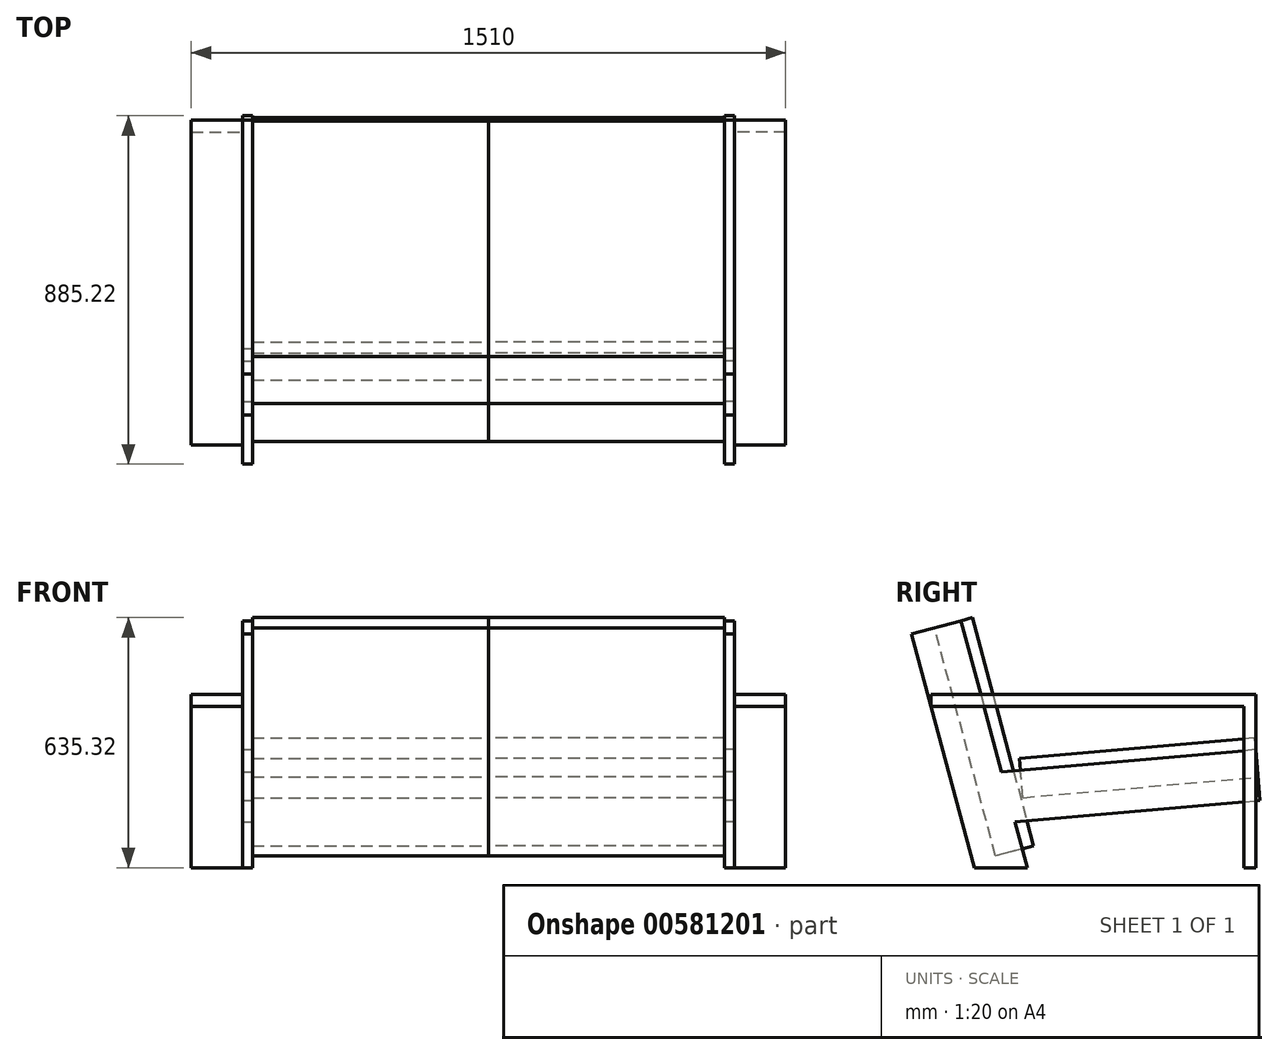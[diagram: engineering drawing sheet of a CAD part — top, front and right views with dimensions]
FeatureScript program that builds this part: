
annotation { "Feature Type Name" : "Feature", "Feature Type Description" : "" }
export const myFeature = defineFeature(function(context is Context, id is Id, definition is map)
    precondition{}
    {
        {
            var Q0;
            Q0=qCreatedBy(makeId("Right.planeOp"),FACE);
            var sketch = newSketch(context, id + "F0", { "sketchPlane" : qUnion([Q0])});
            skLineSegment(sketch, "E0", {"start": v(0, 0) * mm, "end": v(597.72, 52.3) * mm});
            skLineSegment(sketch, "E1", {"start": v(597.72, 52.3) * mm, "end": v(589, 151.91) * mm});
            skLineSegment(sketch, "E2", {"start": v(589, 151.91) * mm, "end": v(-8.72, 99.62) * mm});
            skLineSegment(sketch, "E3", {"start": v(0, 0) * mm, "end": v(-8.72, 99.62) * mm});
            skPoint(sketch, "E4.orphan", {"position": v(0, 100.38) * mm});
            skLineSegment(sketch, "E5", {"start": v(0, 0) * mm, "end": v(456.46, 0) * mm, "construction": true});
            skLineSegment(sketch, "E6", {"start": v(-127.72, 457.35) * mm, "end": v(27.57, -122.2) * mm});
            skLineSegment(sketch, "E7", {"start": v(27.57, -122.2) * mm, "end": v(-69.02, -148.09) * mm});
            skLineSegment(sketch, "E8", {"start": v(-69.02, -148.09) * mm, "end": v(-224.32, 431.47) * mm});
            skLineSegment(sketch, "E9", {"start": v(-127.72, 457.35) * mm, "end": v(-224.32, 431.47) * mm});
            skSolve(sketch);
        }
        {
            var Q0;
            Q0 = qSketchRegion(id + "F0", true);
            extrude(context, id + "F1", {"entities" : qUnion([Q0]), "depth" : 600 * mm, "offsetDistance" : 25 * mm});
        }
        {
            var Q0;
            Q0=makeQuery(id+"F1.opExtrude","CAP_FACE",FACE,{"disambiguationData":[OSD([sQuery(id+"F0.wireOp",EDGE,"E0"),sQuery(id+"F0.wireOp",EDGE,"E1"),sQuery(id+"F0.wireOp",EDGE,"E2"),sQuery(id+"F0.wireOp",EDGE,"E3")])],"isStart":true});
            var sketch = newSketch(context, id + "F2", { "sketchPlane" : qUnion([Q0])});
            skLineSegment(sketch, "E10.0.0", {"start": v(0, 0) * mm, "end": v(8.72, 99.62) * mm});
            skLineSegment(sketch, "E10.0.1", {"start": v(8.72, 99.62) * mm, "end": v(-589, 151.91) * mm});
            skLineSegment(sketch, "E10.0.2", {"start": v(-589, 151.91) * mm, "end": v(-597.72, 52.3) * mm});
            skLineSegment(sketch, "E10.0.3", {"start": v(-597.72, 52.3) * mm, "end": v(0, 0) * mm});
            skLineSegment(sketch, "E11.0.0", {"start": v(127.72, 457.35) * mm, "end": v(-27.57, -122.2) * mm});
            skLineSegment(sketch, "E11.0.1", {"start": v(-27.57, -122.2) * mm, "end": v(69.02, -148.09) * mm});
            skLineSegment(sketch, "E11.0.2", {"start": v(69.02, -148.09) * mm, "end": v(224.32, 431.47) * mm});
            skLineSegment(sketch, "E11.0.3", {"start": v(224.32, 431.47) * mm, "end": v(127.72, 457.35) * mm});
            skSolve(sketch);
        }
        {
            var Q0;
            Q0 = qSketchRegion(id + "F2", true);
            extrude(context, id + "F3", {"entities" : qUnion([Q0]), "depth" : 600 * mm, "offsetDistance" : 25 * mm});
        }
        {
            var Q0;
            Q0=makeQuery(id+"F1.opExtrude","CAP_FACE",FACE,{"disambiguationData":[OSD([sQuery(id+"F0.wireOp",EDGE,"E0"),sQuery(id+"F0.wireOp",EDGE,"E1"),sQuery(id+"F0.wireOp",EDGE,"E2"),sQuery(id+"F0.wireOp",EDGE,"E3")])],"isStart":false});
            var sketch = newSketch(context, id + "F4", { "sketchPlane" : qUnion([Q0])});
            skLineSegment(sketch, "E12", {"start": v(-156.7, 449.59) * mm, "end": v(-282.27, 415.94) * mm});
            skLineSegment(sketch, "E13", {"start": v(-156.7, 449.59) * mm, "end": v(11.45, -177.97) * mm});
            skLineSegment(sketch, "E14", {"start": v(-282.27, 415.94) * mm, "end": v(-123.13, -177.97) * mm});
            skLineSegment(sketch, "E15", {"start": v(-123.13, -177.97) * mm, "end": v(11.45, -177.97) * mm});
            skLineSegment(sketch, "E16", {"start": v(-19.64, -61.95) * mm, "end": v(602.95, -7.48) * mm});
            skLineSegment(sketch, "E17", {"start": v(602.95, -7.48) * mm, "end": v(591.62, 122.03) * mm});
            skLineSegment(sketch, "E18", {"start": v(591.62, 122.03) * mm, "end": v(-53.8, 65.56) * mm});
            skSolve(sketch);
        }
        {
            var Q0;
            Q0 = qSketchRegion(id + "F4", true);
            extrude(context, id + "F5", {"entities" : qUnion([Q0]), "depth" : 25 * mm, "offsetDistance" : 25 * mm});
        }
        {
            var Q0;
            Q0=makeQuery(id+"F5.opExtrude","CAP_FACE",FACE,{"disambiguationData":[OSD([sQuery(id+"F4.wireOp",EDGE,"E12"),sQuery(id+"F4.wireOp",EDGE,"E13"),sQuery(id+"F4.wireOp",EDGE,"E14"),sQuery(id+"F4.wireOp",EDGE,"E15"),sQuery(id+"F4.wireOp",EDGE,"E16"),sQuery(id+"F4.wireOp",EDGE,"E17"),sQuery(id+"F4.wireOp",EDGE,"E18")])],"isStart":false});
            var sketch = newSketch(context, id + "F6", { "sketchPlane" : qUnion([Q0])});
            skLineSegment(sketch, "E19", {"start": v(-233, 232.03) * mm, "end": v(561.62, 232.03) * mm});
            skLineSegment(sketch, "E20", {"start": v(561.62, 232.03) * mm, "end": v(561.62, -177.97) * mm});
            skLineSegment(sketch, "E21", {"start": v(561.62, -177.97) * mm, "end": v(591.62, -177.97) * mm});
            skLineSegment(sketch, "E22", {"start": v(591.62, -177.97) * mm, "end": v(591.62, 262.03) * mm});
            skLineSegment(sketch, "E23", {"start": v(591.62, 262.03) * mm, "end": v(-233, 262.03) * mm});
            skPoint(sketch, "E24.end.orphan", {"position": v(-233, 122.03) * mm});
            skLineSegment(sketch, "E25", {"start": v(-233, 232.03) * mm, "end": v(-233, 262.03) * mm});
            skSolve(sketch);
        }
        {
            var Q0;
            Q0 = qSketchRegion(id + "F6", true);
            extrude(context, id + "F7", {"entities" : qUnion([Q0]), "operationType" : NewBodyOperationType.ADD, "depth" : 130 * mm, "offsetDistance" : 25 * mm});
        }
        {
            var Q0;
            Q0=makeQuery(id+"F5.opExtrude","SWEPT_BODY",BODY,{"disambiguationData":[OSD([sQuery(id+"F4.wireOp",EDGE,"E12"),sQuery(id+"F4.wireOp",EDGE,"E13"),sQuery(id+"F4.wireOp",EDGE,"E14"),sQuery(id+"F4.wireOp",EDGE,"E15"),sQuery(id+"F4.wireOp",EDGE,"E16"),sQuery(id+"F4.wireOp",EDGE,"E17"),sQuery(id+"F4.wireOp",EDGE,"E18")])]});
            var Q1;
            Q1=qCreatedBy(makeId("Right.planeOp"),FACE);
            mirror(context, id + "F8", {"entities" : qUnion([Q0]), "mirrorPlane" : qUnion([Q1])});
        }
    });
